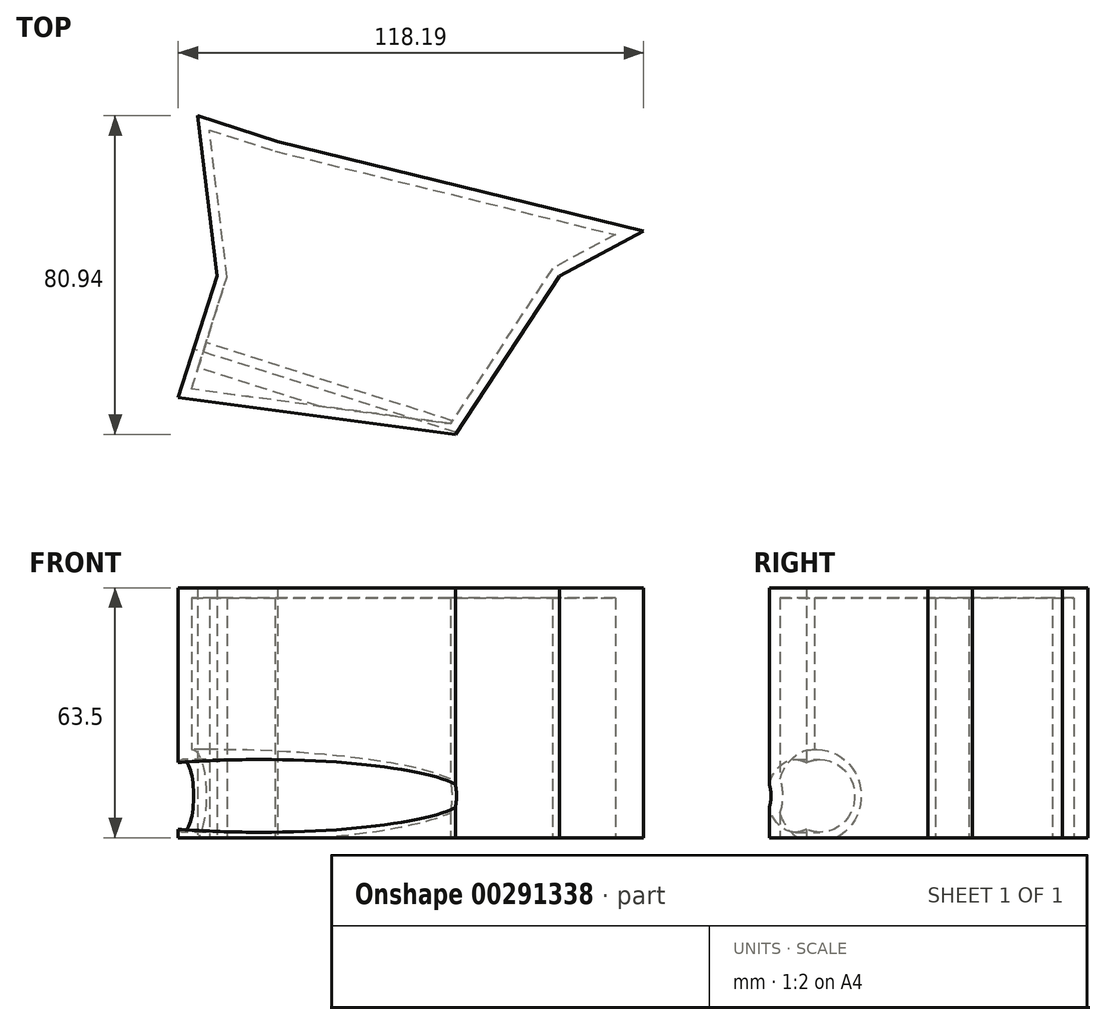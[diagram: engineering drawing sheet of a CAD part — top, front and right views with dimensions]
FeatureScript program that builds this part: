
annotation { "Feature Type Name" : "Feature", "Feature Type Description" : "" }
export const myFeature = defineFeature(function(context is Context, id is Id, definition is map)
    precondition{}
    {
        {
            var Q0;
            Q0=qCreatedBy(makeId("Top.planeOp"),FACE);
            var sketch = newSketch(context, id + "F0", { "sketchPlane" : qUnion([Q0])});
            skLineSegment(sketch, "E0", {"start": v(-19.1, 33.03) * mm, "end": v(73.82, 10.22) * mm});
            skLineSegment(sketch, "E1", {"start": v(73.82, 10.22) * mm, "end": v(52.48, -1.12) * mm});
            skLineSegment(sketch, "E2", {"start": v(52.48, -1.12) * mm, "end": v(26.05, -41.36) * mm});
            skLineSegment(sketch, "E3", {"start": v(26.05, -41.36) * mm, "end": v(-44.37, -32) * mm});
            skLineSegment(sketch, "E4", {"start": v(-44.37, -32) * mm, "end": v(-34.55, -1.12) * mm});
            skLineSegment(sketch, "E5", {"start": v(-34.55, -1.12) * mm, "end": v(-39.46, 39.58) * mm});
            skLineSegment(sketch, "E6", {"start": v(-39.46, 39.58) * mm, "end": v(-19.1, 33.03) * mm});
            skSolve(sketch);
        }
        {
            var Q0;
            Q0 = qSketchRegion(id + "F0", true);
            extrude(context, id + "F1", {"entities" : qUnion([Q0]), "depth" : 63.5 * mm});
        }
        {
            var Q0;
            Q0=makeQuery(id+"F1.opExtrude","SWEPT_FACE",FACE,{"disambiguationData":[OSD([sQuery(id+"F0.wireOp",EDGE,"E4")])]});
            var sketch = newSketch(context, id + "F2", { "sketchPlane" : qUnion([Q0])});
            skCircle(sketch, "E7", {"center": v(40.26, 10.63) * mm, "radius": 9.23 * mm});
            skSolve(sketch);
        }
        {
            var Q0;
            Q0 = qSketchRegion(id + "F2", true);
            extrude(context, id + "F3", {"entities" : qUnion([Q0]), "operationType" : NewBodyOperationType.REMOVE, "endBound" : BoundingType.THROUGH_ALL, "oppositeDirection" : true, "depth" : 6.35 * mm});
        }
        {
            var Q0;
            Q0=makeQuery(id+"F1.opExtrude","CAP_FACE",FACE,{"disambiguationData":[OSD([sQuery(id+"F0.wireOp",EDGE,"E0"),sQuery(id+"F0.wireOp",EDGE,"E1"),sQuery(id+"F0.wireOp",EDGE,"E2"),sQuery(id+"F0.wireOp",EDGE,"E3"),sQuery(id+"F0.wireOp",EDGE,"E4"),sQuery(id+"F0.wireOp",EDGE,"E5"),sQuery(id+"F0.wireOp",EDGE,"E6")])],"isStart":true});
            shell(context, id + "F4", {"entities" : qUnion([Q0]), "thickness" : 2.54 * mm});
        }
    });
